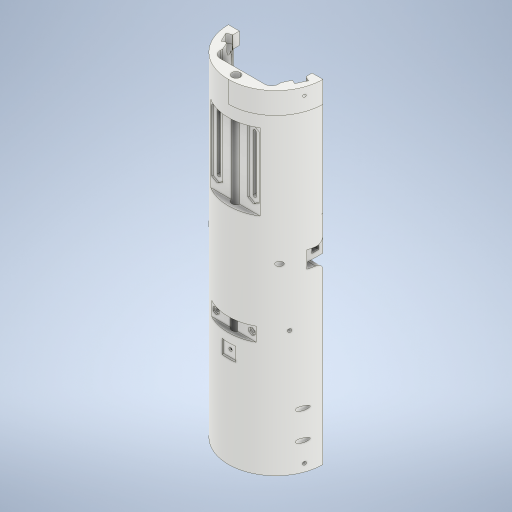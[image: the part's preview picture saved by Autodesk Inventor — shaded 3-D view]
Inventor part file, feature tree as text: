
AUTODESK INVENTOR PART (.ipt)
format: ipt  version: 2023 (Build 270158030, 158C)  size: 677,888 bytes
history: mixed  units: in
note: dims shown in document units (in); Inventor stores cm internally (conversion verified against a paired STEP export)
features: move_body x28, direct_edit x7, extrude x5, sketch x5, other x1, imported_body x1
ambient origin geometry x8: Origin, YZ Plane, XZ Plane, XY Plane, X Axis, Y Axis, Z Axis, Center Point
bodies: Solid42 (imported_parasolid)
feature tree (47):
  other  "Base (1) (1)"
  direct_edit  "Direct Edit1"
  direct_edit  "Direct Edit2"
  extrude  "Extrusion1"  Depth=0.9843in TaperAngle=0.0deg
  extrude  "Extrusion2"  Depth=0.0787in
  extrude  "Extrusion3"  Depth=0.1453in
  sketch  "Sketch4"  dims[d12=0.0in d13=0.0in d14=0.0in d15=0.0in]
  direct_edit  "Direct Edit3"
  extrude  "Extrusion4"  TaperAngle=0.0deg  [1 undecoded]
  direct_edit  "Direct Edit4"
  direct_edit  "Direct Edit5"
  extrude  "Extrusion5"  Depth=1.5748in
  direct_edit  "Direct Edit6"
  direct_edit  "Direct Edit7"
  sketch  "Sketch1"  dims[d0=0.0in d1=0.0in d2=0.9843in d3=0.0in d4=0.9843in d5=0.0in]
  sketch  "Sketch2"  dims[d6=0.0in d7=0.9843in d8=0.0in d9=0.0787in]
  sketch  "Sketch3"  dims[d10=0.217in d11=0.1453in]
  sketch  "Sketch5"  dims[d16=0.0in d17=0.0in d18=1.5748in d19=0.0906in d20=0.0906in d21=0.0in d22=0.0in d23=-1.7717in d24=0.0in d25=-1.5748in d26=0.0in d27=0.0in d28=-1.5748in d29=0.0in d30=0.0in d31=0.0in d32=0.0in d33=0.0in d34=-0.0709in d35=0.0in d36=0.0in d37=-0.0709in d38=0.0in d39=0.0in d40=-0.0709in d41=0.0in d42=0.0in d43=-0.0709in d44=0.0in d45=0.0in d46=-0.0709in d47=0.0in d48=0.0in d49=-0.0709in d50=0.0in d51=0.0in d52=-0.0709in d53=0.0in d54=0.0in d55=-0.0709in d56=0.0in d57=0.0in d58=-0.0709in d59=0.0in d60=0.0in d61=-0.0709in d62=0.0in d63=0.0in d64=-0.0709in d65=0.0in d66=0.0in d67=-0.0709in d68=0.1181in d69=0.7874in d70=0.1181in d71=0.7874in d72=0.1181in d73=0.7874in d74=0.1181in d75=0.7874in d76=0.0in d77=0.0in d78=0.0in d79=0.0in d80=0.0709in d81=0.0in d82=0.0in d83=0.0709in d86=0.0in d87=0.0in d88=0.0787in d89=0.0in d90=0.0in d91=0.0787in d92=0.0in d93=0.0in d94=-0.0787in d95=0.0in d96=0.0in d97=-0.0787in d98=0.0in d99=0.0in d100=0.0787in d101=0.0in d102=0.0in d103=0.0787in d104=0.0in d105=0.0in d106=0.1732in d107=0.0in d108=0.0in d109=0.1732in]
  move_body  "Move1"
  move_body  "Move2"
  move_body  "Move3"
  move_body  "Move4"
  move_body  "Move5"
  move_body  "Move6"
  move_body  "Move7"
  move_body  "Move8"
  move_body  "Move9"
  move_body  "Move10"
  move_body  "Move11"
  move_body  "Move12"
  move_body  "Move13"
  move_body  "Move14"
  move_body  "Move15"
  move_body  "Move16"
  move_body  "Move17"
  move_body  "Move18"
  move_body  "Move19"
  move_body  "Move20"
  move_body  "Move21"
  move_body  "Move22"
  move_body  "Move23"
  move_body  "Move24"
  move_body  "Move25"
  move_body  "Move26"
  move_body  "Move27"
  move_body  "Move28"
  imported_body  NMx_Import_Brep_tag  [imported B-rep: ~8 faces, bbox_mm=[0.0, 0.0, 0.0]]
note: 1 required parameter value undecoded (feature->parameter linkage not recoverable at this tier; creation-order binding heuristic only, values carry confidence <= 0.55)
